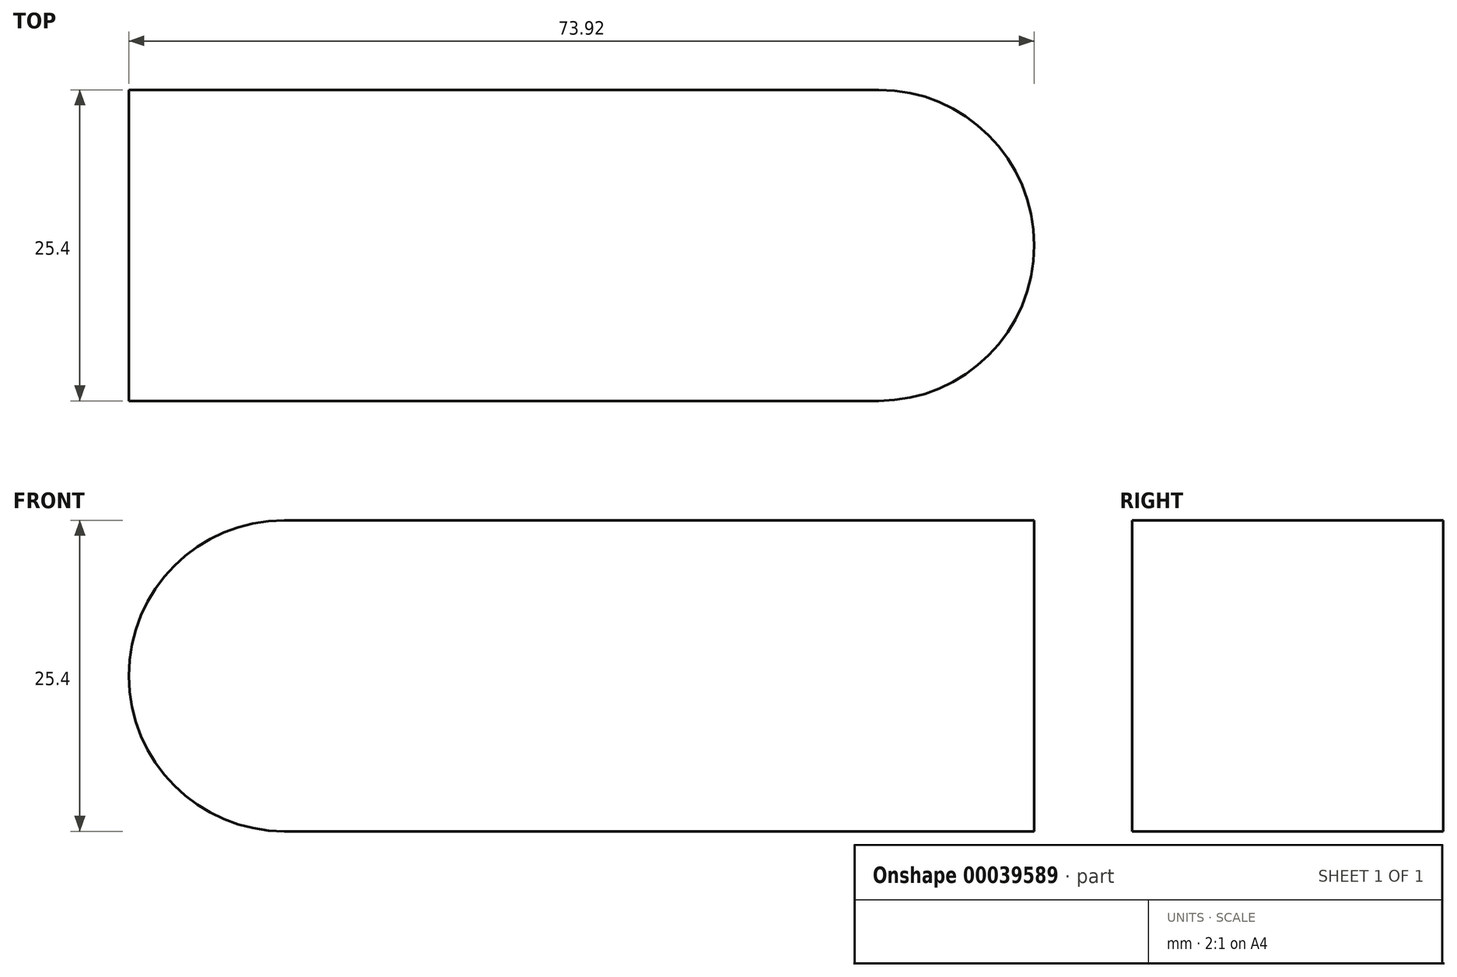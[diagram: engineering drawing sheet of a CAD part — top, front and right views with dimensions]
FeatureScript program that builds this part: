
annotation { "Feature Type Name" : "Feature", "Feature Type Description" : "" }
export const myFeature = defineFeature(function(context is Context, id is Id, definition is map)
    precondition{}
    {
        {
            var Q0;
            Q0=qCreatedBy(makeId("Front.planeOp"),FACE);
            var sketch = newSketch(context, id + "F0", { "sketchPlane" : qUnion([Q0])});
            skLineSegment(sketch, "E0", {"start": v(0, 25.4) * mm, "end": v(48.52, 25.4) * mm});
            skLineSegment(sketch, "E1", {"start": v(48.52, 25.4) * mm, "end": v(48.52, 0) * mm});
            skLineSegment(sketch, "E2", {"start": v(48.52, 0) * mm, "end": v(0, 0) * mm});
            skArc(sketch, "E3", {"start": v(0, 25.4) * mm, "mid": v(-12.7, 12.7) * mm, "end": v(0, 0) * mm});
            skSolve(sketch);
        }
        {
            var Q0;
            Q0=makeQuery(id+"F0.imprint","IMPRINT",FACE,{"disambiguationData":[TD([[makeQuery(id+"F0.imprint","IMPRINT",EDGE,{"derivedFrom":sQuery(id+"F0.wireOp",EDGE,"E0")}),-1.0]])]});
            extrude(context, id + "F1", {"entities" : qUnion([Q0]), "depth" : 25.4 * mm});
        }
        {
            var Q0;
            Q0=makeQuery(id+"F1.opExtrude","SWEPT_FACE",FACE,{"disambiguationData":[OSD([sQuery(id+"F0.wireOp",EDGE,"E0")])]});
            var sketch = newSketch(context, id + "F2", { "sketchPlane" : qUnion([Q0])});
            skPoint(sketch, "E4.center.orphan", {"position": v(48.52, -12.7) * mm});
            skArc(sketch, "E5", {"start": v(48.52, -25.4) * mm, "mid": v(61.22, -12.7) * mm, "end": v(48.52, 0) * mm});
            skLineSegment(sketch, "E6", {"start": v(48.52, 0) * mm, "end": v(48.52, -25.4) * mm});
            skSolve(sketch);
        }
        {
            var Q0;
            Q0 = qSketchRegion(id + "F2", true);
            var Q1;
            Q1=makeQuery(id+"F1.opExtrude","SWEPT_FACE",FACE,{"disambiguationData":[OSD([sQuery(id+"F0.wireOp",EDGE,"E2")])]});
            extrude(context, id + "F3", {"entities" : qUnion([Q0]), "operationType" : NewBodyOperationType.ADD, "endBound" : BoundingType.UP_TO_SURFACE, "oppositeDirection" : true, "endBoundEntityFace" : qUnion([Q1]), "depth" : 25.4 * mm});
        }
    });
